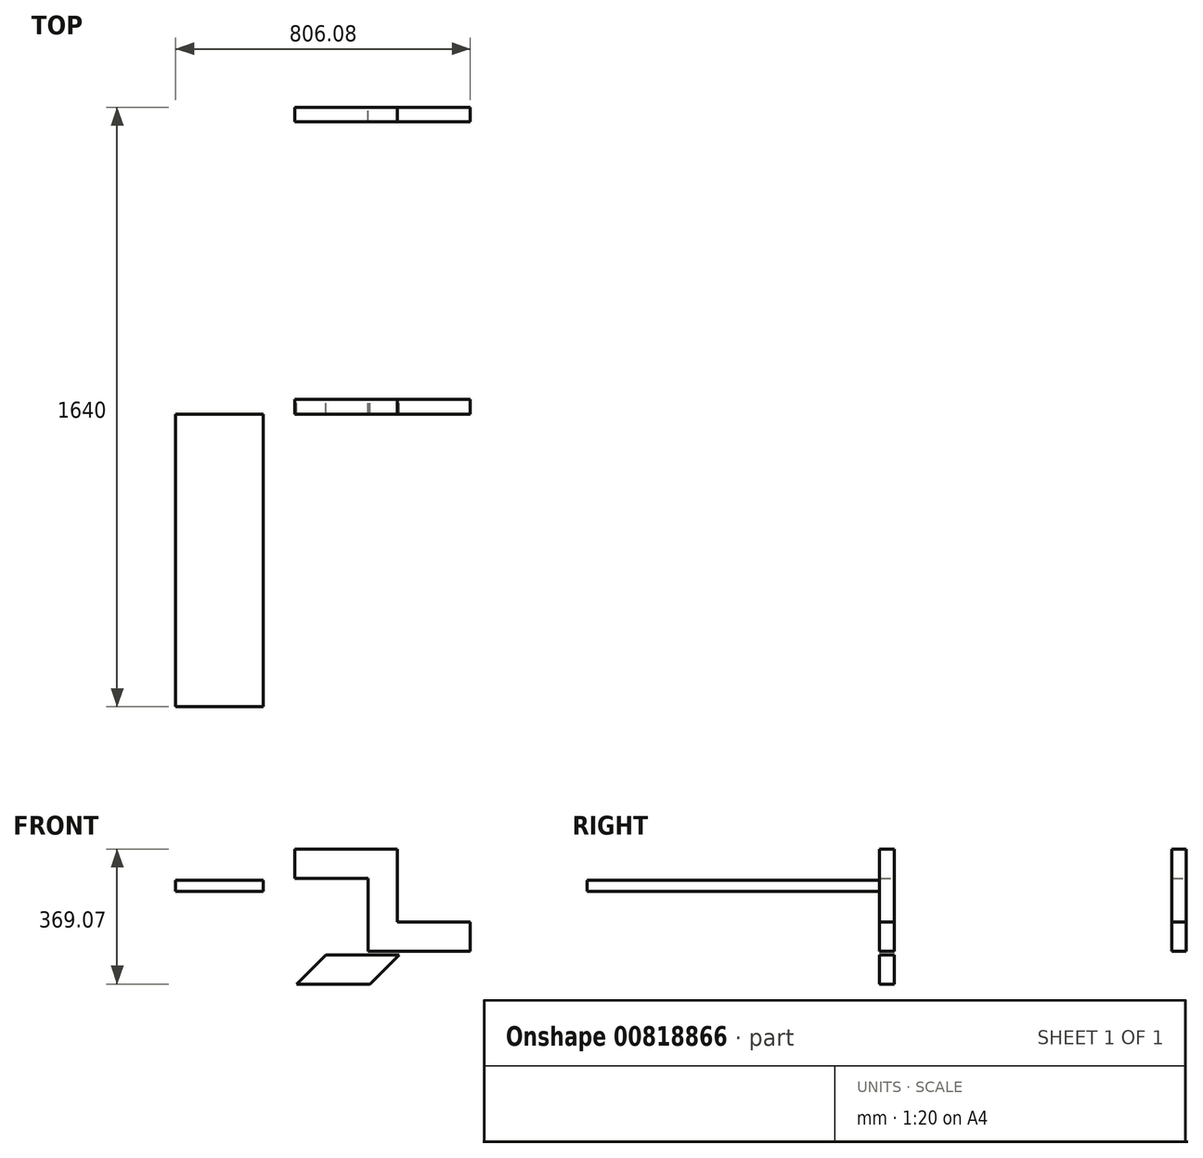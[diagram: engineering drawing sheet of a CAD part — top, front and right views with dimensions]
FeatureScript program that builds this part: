
annotation { "Feature Type Name" : "Feature", "Feature Type Description" : "" }
export const myFeature = defineFeature(function(context is Context, id is Id, definition is map)
    precondition{}
    {
        {
            var Q0;
            Q0=qCreatedBy(makeId("Front.planeOp"),FACE);
            var sketch = newSketch(context, id + "F0", { "sketchPlane" : qUnion([Q0])});
            skLineSegment(sketch, "E0.bottom", {"start": v(0, 0) * mm, "end": v(200, 0) * mm});
            skLineSegment(sketch, "E0.top", {"start": v(0, 80) * mm, "end": v(200, 80) * mm});
            skLineSegment(sketch, "E0.right", {"start": v(200, 0) * mm, "end": v(200, 80) * mm});
            skLineSegment(sketch, "E1.bottom", {"start": v(0, 0) * mm, "end": v(-80, 0) * mm});
            skLineSegment(sketch, "E1.top", {"start": v(0, 280) * mm, "end": v(-80, 280) * mm});
            skLineSegment(sketch, "E1.left", {"start": v(0, 80) * mm, "end": v(0, 280) * mm});
            skLineSegment(sketch, "E1.right", {"start": v(-80, 0) * mm, "end": v(-80, 200) * mm});
            skLineSegment(sketch, "E2", {"start": v(0, 80) * mm, "end": v(-80, 0) * mm});
            skLineSegment(sketch, "E3.bottom", {"start": v(-80, 280) * mm, "end": v(-280, 280) * mm});
            skLineSegment(sketch, "E3.top", {"start": v(-80, 200) * mm, "end": v(-280, 200) * mm});
            skLineSegment(sketch, "E3.right", {"start": v(-280, 280) * mm, "end": v(-280, 200) * mm});
            skLineSegment(sketch, "E4", {"start": v(-80, 200) * mm, "end": v(0, 280) * mm});
            skSolve(sketch);
        }
        {
            var Q0;
            Q0=makeQuery(id+"F0.imprint","IMPRINT",FACE,{"disambiguationData":[TD([[makeQuery(id+"F0.imprint","IMPRINT",EDGE,{"derivedFrom":sQuery(id+"F0.wireOp",EDGE,"E1.left")}),1.0]])]});
            var Q1;
            Q1=makeQuery(id+"F0.imprint","IMPRINT",FACE,{"disambiguationData":[TD([[makeQuery(id+"F0.imprint","IMPRINT",EDGE,{"derivedFrom":sQuery(id+"F0.wireOp",EDGE,"E1.top")}),1.0]])]});
            var Q2;
            Q2=makeQuery(id+"F0.imprint","IMPRINT",FACE,{"disambiguationData":[TD([[makeQuery(id+"F0.imprint","IMPRINT",EDGE,{"derivedFrom":sQuery(id+"F0.wireOp",EDGE,"E0.bottom")}),1.0]])]});
            extrude(context, id + "F1", {"entities" : qUnion([Q0, Q1, Q2]), "depth" : 40 * mm, "offsetDistance" : 25 * mm});
        }
        {
            var Q0;
            Q0=makeQuery(id+"F1.opExtrude","SWEPT_BODY",BODY,{"disambiguationData":[OSD([sQuery(id+"F0.wireOp",EDGE,"E0.bottom"),sQuery(id+"F0.wireOp",EDGE,"E0.top"),sQuery(id+"F0.wireOp",EDGE,"E0.right"),sQuery(id+"F0.wireOp",EDGE,"E1.bottom"),sQuery(id+"F0.wireOp",EDGE,"E1.top"),sQuery(id+"F0.wireOp",EDGE,"E1.left"),sQuery(id+"F0.wireOp",EDGE,"E1.right"),sQuery(id+"F0.wireOp",EDGE,"E3.bottom"),sQuery(id+"F0.wireOp",EDGE,"E3.top"),sQuery(id+"F0.wireOp",EDGE,"E3.right")])]});
            transform(context, id + "F2", {"entities" : qUnion([Q0]), "transformType" : TransformType.TRANSLATION_3D, "dx" : 0 * mm, "dy" : 800 * mm, "dz" : 0 * mm, "makeCopy" : true});
        }
        {
            var Q0;
            Q0=makeQuery(id+"F1.opExtrude","CAP_FACE",FACE,{"disambiguationData":[OSD([sQuery(id+"F0.wireOp",EDGE,"E0.bottom"),sQuery(id+"F0.wireOp",EDGE,"E0.top"),sQuery(id+"F0.wireOp",EDGE,"E0.right"),sQuery(id+"F0.wireOp",EDGE,"E1.bottom"),sQuery(id+"F0.wireOp",EDGE,"E1.top"),sQuery(id+"F0.wireOp",EDGE,"E1.left"),sQuery(id+"F0.wireOp",EDGE,"E1.right"),sQuery(id+"F0.wireOp",EDGE,"E3.bottom"),sQuery(id+"F0.wireOp",EDGE,"E3.top"),sQuery(id+"F0.wireOp",EDGE,"E3.right")])],"isStart":false});
            var sketch = newSketch(context, id + "F3", { "sketchPlane" : qUnion([Q0])});
            skLineSegment(sketch, "E5.bottom", {"start": v(-606.08, 194.94) * mm, "end": v(-366.08, 194.94) * mm});
            skLineSegment(sketch, "E5.top", {"start": v(-606.08, 164.94) * mm, "end": v(-366.08, 164.94) * mm});
            skLineSegment(sketch, "E5.left", {"start": v(-606.08, 194.94) * mm, "end": v(-606.08, 164.94) * mm});
            skLineSegment(sketch, "E5.right", {"start": v(-366.08, 194.94) * mm, "end": v(-366.08, 164.94) * mm});
            skSolve(sketch);
        }
        {
            var Q0;
            Q0 = qSketchRegion(id + "F3", true);
            extrude(context, id + "F4", {"entities" : qUnion([Q0]), "depth" : 800 * mm, "offsetDistance" : 25 * mm});
        }
        {
            var Q0;
            Q0=makeQuery(id+"F4.opExtrude","SWEPT_BODY",BODY,{"disambiguationData":[OSD([sQuery(id+"F3.wireOp",EDGE,"E5.bottom"),sQuery(id+"F3.wireOp",EDGE,"E5.top"),sQuery(id+"F3.wireOp",EDGE,"E5.left"),sQuery(id+"F3.wireOp",EDGE,"E5.right")])]});
            var Q1;
            Q1=makeQuery(id+"F2.opPattern","COPY",BODY,{"derivedFrom":makeQuery(id+"F1.opExtrude","SWEPT_BODY",BODY,{"disambiguationData":[OSD([sQuery(id+"F0.wireOp",EDGE,"E0.bottom"),sQuery(id+"F0.wireOp",EDGE,"E0.top"),sQuery(id+"F0.wireOp",EDGE,"E0.right"),sQuery(id+"F0.wireOp",EDGE,"E1.bottom"),sQuery(id+"F0.wireOp",EDGE,"E1.top"),sQuery(id+"F0.wireOp",EDGE,"E1.left"),sQuery(id+"F0.wireOp",EDGE,"E1.right"),sQuery(id+"F0.wireOp",EDGE,"E3.bottom"),sQuery(id+"F0.wireOp",EDGE,"E3.top"),sQuery(id+"F0.wireOp",EDGE,"E3.right")])]}),"instanceName":"1"});
            transform(context, id + "F5", {"entities" : qUnion([Q0, Q1]), "transformType" : TransformType.COPY});
        }
        {
            var Q0;
            Q0=makeQuery(id+"F5.opPattern","COPY",BODY,{"derivedFrom":makeQuery(id+"F4.opExtrude","SWEPT_BODY",BODY,{"disambiguationData":[OSD([sQuery(id+"F3.wireOp",EDGE,"E5.bottom"),sQuery(id+"F3.wireOp",EDGE,"E5.top"),sQuery(id+"F3.wireOp",EDGE,"E5.left"),sQuery(id+"F3.wireOp",EDGE,"E5.right")])]}),"instanceName":"1"});
            var Q1;
            Q1=makeQuery(id+"F5.opPattern","COPY",BODY,{"derivedFrom":makeQuery(id+"F2.opPattern","COPY",BODY,{"derivedFrom":makeQuery(id+"F1.opExtrude","SWEPT_BODY",BODY,{"disambiguationData":[OSD([sQuery(id+"F0.wireOp",EDGE,"E0.bottom"),sQuery(id+"F0.wireOp",EDGE,"E0.top"),sQuery(id+"F0.wireOp",EDGE,"E0.right"),sQuery(id+"F0.wireOp",EDGE,"E1.bottom"),sQuery(id+"F0.wireOp",EDGE,"E1.top"),sQuery(id+"F0.wireOp",EDGE,"E1.left"),sQuery(id+"F0.wireOp",EDGE,"E1.right"),sQuery(id+"F0.wireOp",EDGE,"E3.bottom"),sQuery(id+"F0.wireOp",EDGE,"E3.top"),sQuery(id+"F0.wireOp",EDGE,"E3.right")])]}),"instanceName":"1"}),"instanceName":"1"});
            deleteBodies(context, id + "F6", {"entities" : qUnion([Q0, Q1])});
        }
        {
            var Q0;
            Q0=qCreatedBy(makeId("Front.planeOp"),FACE);
            var sketch = newSketch(context, id + "F7", { "sketchPlane" : qUnion([Q0])});
            skLineSegment(sketch, "E6.bottom", {"start": v(-194.77, -89.07) * mm, "end": v(-74.77, -89.07) * mm});
            skLineSegment(sketch, "E6.top", {"start": v(-194.77, -9.07) * mm, "end": v(5.23, -9.07) * mm});
            skLineSegment(sketch, "E6.left", {"start": v(-194.77, -89.07) * mm, "end": v(-194.77, -9.07) * mm});
            skLineSegment(sketch, "E7.bottom", {"start": v(-194.77, -89.07) * mm, "end": v(-274.77, -89.07) * mm});
            skLineSegment(sketch, "E8", {"start": v(-194.77, -9.07) * mm, "end": v(-274.77, -89.07) * mm});
            skLineSegment(sketch, "E9", {"start": v(-74.77, -89.07) * mm, "end": v(5.23, -9.07) * mm});
            skSolve(sketch);
        }
        {
            var Q0;
            Q0=makeQuery(id+"F7.imprint","IMPRINT",FACE,{"disambiguationData":[TD([[makeQuery(id+"F7.imprint","IMPRINT",EDGE,{"derivedFrom":sQuery(id+"F7.wireOp",EDGE,"E6.bottom")}),1.0]])]});
            var Q1;
            Q1=makeQuery(id+"F7.imprint","IMPRINT",FACE,{"disambiguationData":[TD([[makeQuery(id+"F7.imprint","IMPRINT",EDGE,{"derivedFrom":sQuery(id+"F7.wireOp",EDGE,"E7.bottom")}),-1.0]])]});
            extrude(context, id + "F8", {"entities" : qUnion([Q0, Q1]), "depth" : 40 * mm, "offsetDistance" : 25 * mm});
        }
    });
